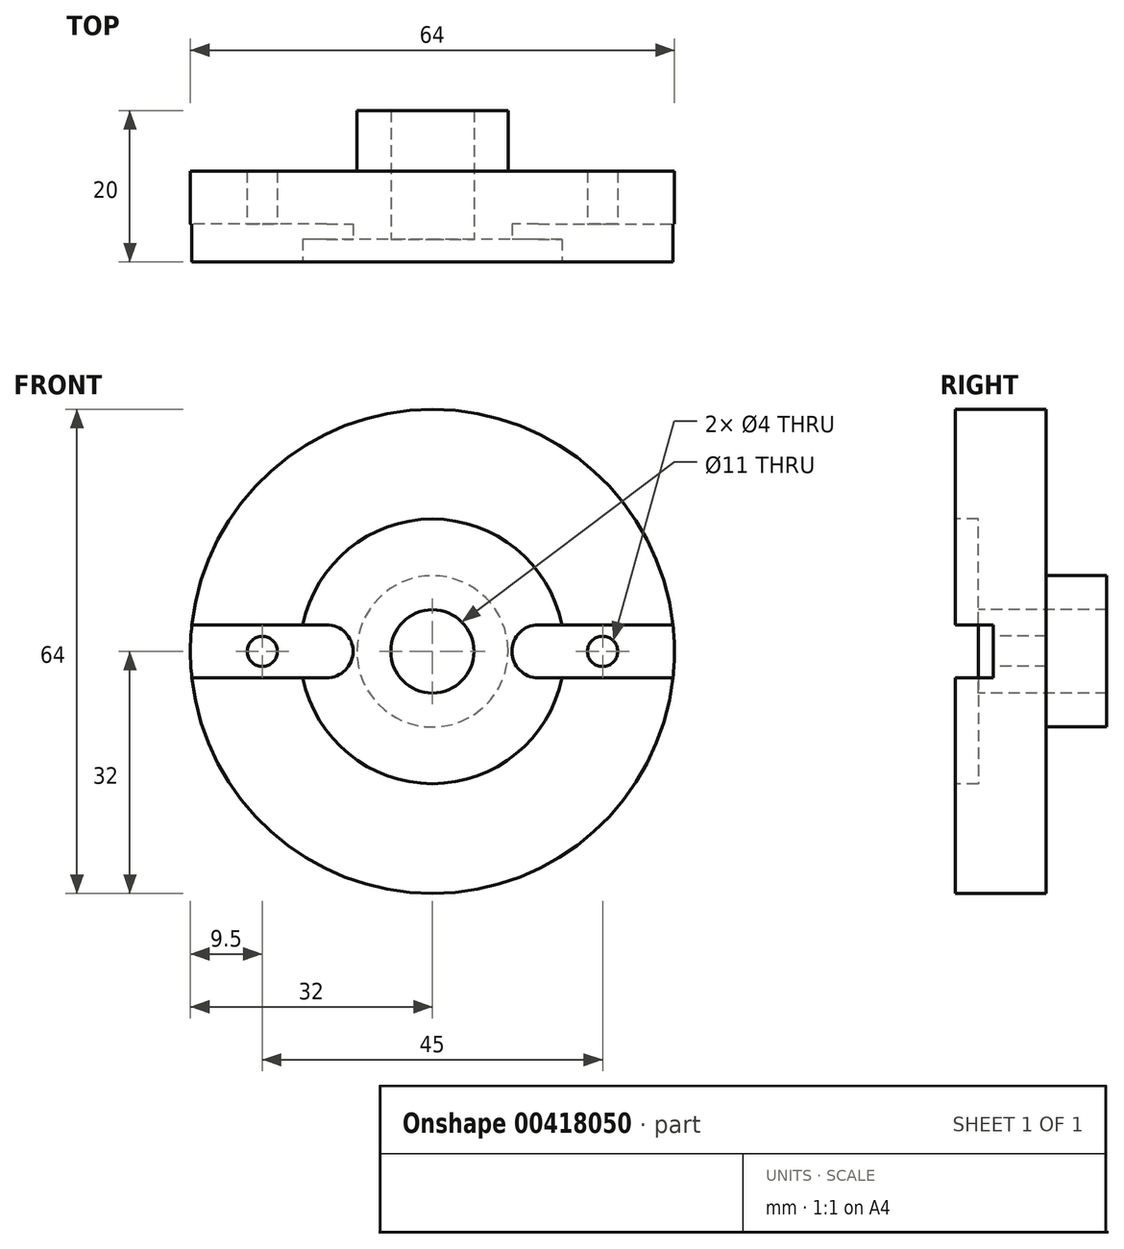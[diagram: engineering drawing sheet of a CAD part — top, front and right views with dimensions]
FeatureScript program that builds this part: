
annotation { "Feature Type Name" : "Feature", "Feature Type Description" : "" }
export const myFeature = defineFeature(function(context is Context, id is Id, definition is map)
    precondition{}
    {
        {
            var Q0;
            Q0=qCreatedBy(makeId("Front.planeOp"),FACE);
            var sketch = newSketch(context, id + "F0", { "sketchPlane" : qUnion([Q0])});
            skCircle(sketch, "E0", {"center": v(0, 0) * mm, "radius": 32 * mm});
            skSolve(sketch);
        }
        {
            var Q0;
            Q0=makeQuery(id+"F0.imprint","IMPRINT",FACE,{"disambiguationData":[TD([[makeQuery(id+"F0.imprint","IMPRINT",EDGE,{"derivedFrom":sQuery(id+"F0.wireOp",EDGE,"E0")}),1.0]])]});
            extrude(context, id + "F1", {"entities" : qUnion([Q0]), "oppositeDirection" : true, "depth" : 20 * mm});
        }
        {
            var Q0;
            Q0=qCreatedBy(makeId("Front.planeOp"),FACE);
            var sketch = newSketch(context, id + "F2", { "sketchPlane" : qUnion([Q0])});
            skCircle(sketch, "E1", {"center": v(0, 0) * mm, "radius": 17.5 * mm});
            skSolve(sketch);
        }
        {
            var Q0;
            Q0 = qSketchRegion(id + "F2", true);
            extrude(context, id + "F3", {"entities" : qUnion([Q0]), "operationType" : NewBodyOperationType.REMOVE, "oppositeDirection" : true, "depth" : 3 * mm});
        }
        {
            var Q0;
            Q0=makeQuery(id+"F1.opExtrude","CAP_FACE",FACE,{"disambiguationData":[OSD([sQuery(id+"F0.wireOp",EDGE,"E0")])],"isStart":true});
            var sketch = newSketch(context, id + "F4", { "sketchPlane" : qUnion([Q0])});
            skLineSegment(sketch, "E2.bottom", {"start": v(14, 3.5) * mm, "end": v(32, 3.5) * mm});
            skLineSegment(sketch, "E2.top", {"start": v(14, -3.5) * mm, "end": v(32, -3.5) * mm});
            skLineSegment(sketch, "E2.right", {"start": v(32, 3.5) * mm, "end": v(32, -3.5) * mm});
            skArc(sketch, "E3", {"start": v(14, 3.5) * mm, "mid": v(10.5, 0) * mm, "end": v(14, -3.5) * mm});
            skArc(sketch, "E4.MirrorCS", {"start": v(-14, 3.5) * mm, "mid": v(-10.5, 0) * mm, "end": v(-14, -3.5) * mm});
            skLineSegment(sketch, "E5.MirrorCS", {"start": v(-14, 3.5) * mm, "end": v(-32, 3.5) * mm});
            skLineSegment(sketch, "E6.MirrorCS", {"start": v(-14, -3.5) * mm, "end": v(-32, -3.5) * mm});
            skLineSegment(sketch, "E7.MirrorCS", {"start": v(-32, 3.5) * mm, "end": v(-32, -3.5) * mm});
            skSolve(sketch);
        }
        {
            var Q0;
            Q0 = qSketchRegion(id + "F4", true);
            extrude(context, id + "F5", {"entities" : qUnion([Q0]), "operationType" : NewBodyOperationType.REMOVE, "oppositeDirection" : true, "depth" : 5 * mm});
        }
        {
            var Q0;
            Q0=makeQuery(id+"F1.opExtrude","CAP_FACE",FACE,{"disambiguationData":[OSD([sQuery(id+"F0.wireOp",EDGE,"E0")])],"isStart":false});
            var sketch = newSketch(context, id + "F6", { "sketchPlane" : qUnion([Q0])});
            skCircle(sketch, "E8", {"center": v(0, 0) * mm, "radius": 37.03 * mm});
            skCircle(sketch, "E9", {"center": v(0, 0) * mm, "radius": 10 * mm});
            skSolve(sketch);
        }
        {
            var Q0;
            Q0=makeQuery(id+"F6.imprint","IMPRINT",FACE,{"disambiguationData":[TD([[makeQuery(id+"F6.imprint","IMPRINT",EDGE,{"derivedFrom":sQuery(id+"F6.wireOp",EDGE,"E9")}),-1.0]])]});
            extrude(context, id + "F7", {"entities" : qUnion([Q0]), "operationType" : NewBodyOperationType.REMOVE, "oppositeDirection" : true, "depth" : 8 * mm});
        }
        {
            var Q0;
            Q0=makeQuery(id+"F3.boolean.opBoolean","COPY",FACE,{"derivedFrom":makeQuery(id+"F3.opExtrude","CAP_FACE",FACE,{"disambiguationData":[OSD([sQuery(id+"F2.wireOp",EDGE,"E1")])],"isStart":false})});
            var sketch = newSketch(context, id + "F8", { "sketchPlane" : qUnion([Q0])});
            skCircle(sketch, "E10", {"center": v(0, 0) * mm, "radius": 5.5 * mm});
            skSolve(sketch);
        }
        {
            var Q0;
            Q0 = qSketchRegion(id + "F8", true);
            extrude(context, id + "F9", {"entities" : qUnion([Q0]), "operationType" : NewBodyOperationType.REMOVE, "endBound" : BoundingType.THROUGH_ALL, "oppositeDirection" : true, "depth" : 25 * mm});
        }
        {
            var Q0;
            Q0=qCreatedBy(makeId("Front.planeOp"),FACE);
            var sketch = newSketch(context, id + "F10", { "sketchPlane" : qUnion([Q0])});
            skCircle(sketch, "E11", {"center": v(-22.5, 0) * mm, "radius": 2 * mm});
            skCircle(sketch, "E12.MirrorC", {"center": v(22.5, 0) * mm, "radius": 2 * mm});
            skSolve(sketch);
        }
        {
            var Q0;
            Q0 = qSketchRegion(id + "F10", true);
            extrude(context, id + "F11", {"entities" : qUnion([Q0]), "operationType" : NewBodyOperationType.REMOVE, "endBound" : BoundingType.THROUGH_ALL, "oppositeDirection" : true, "depth" : 25 * mm});
        }
    });
